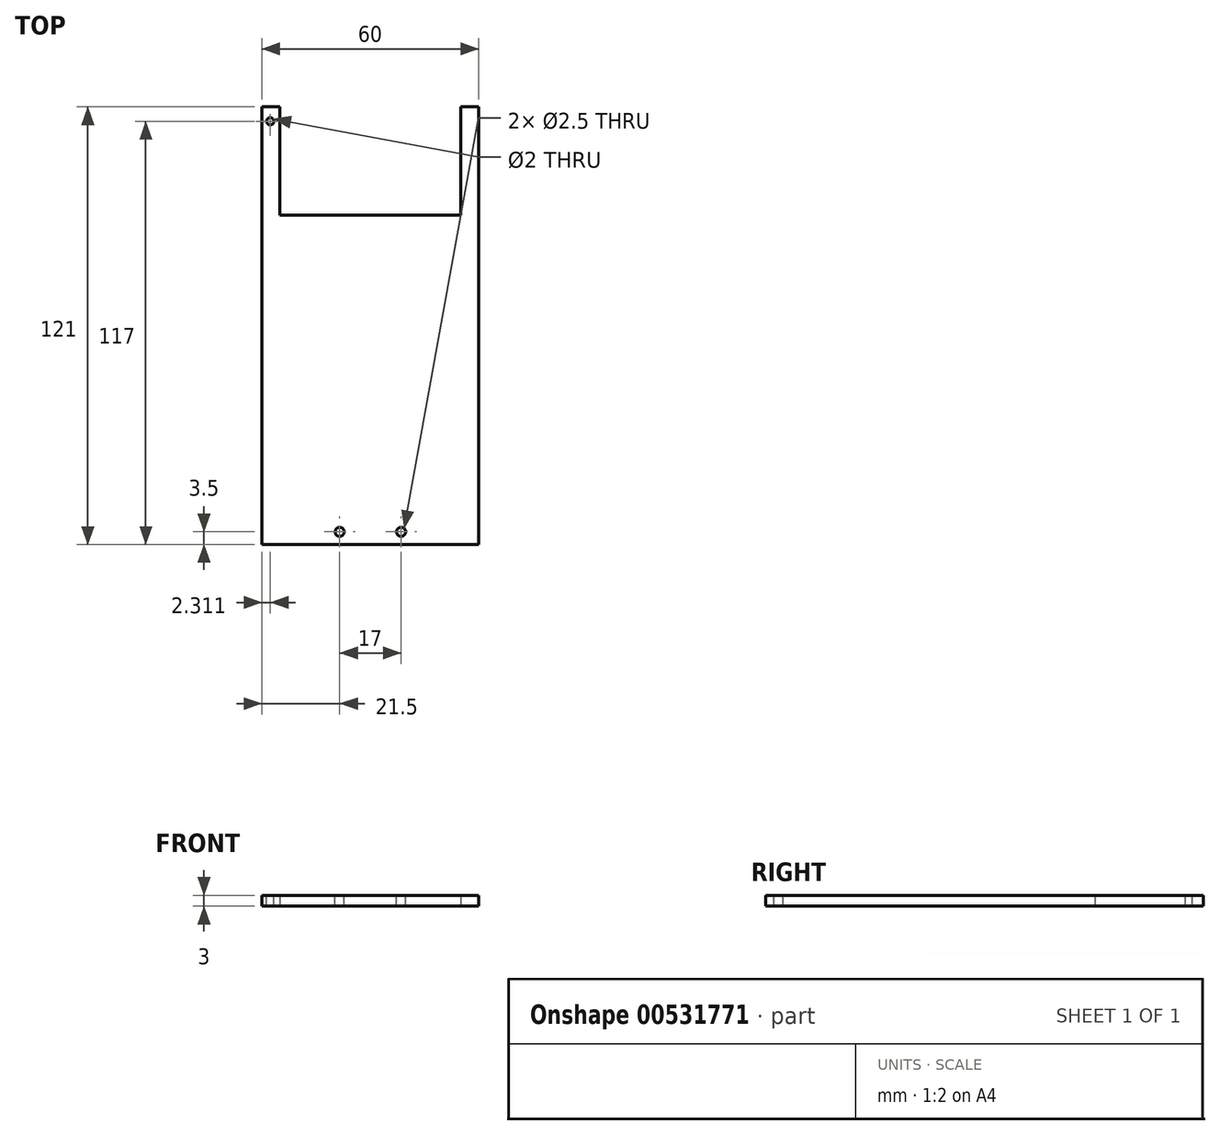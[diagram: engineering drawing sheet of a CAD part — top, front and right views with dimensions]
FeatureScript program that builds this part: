
annotation { "Feature Type Name" : "Feature", "Feature Type Description" : "" }
export const myFeature = defineFeature(function(context is Context, id is Id, definition is map)
    precondition{}
    {
        {
            var Q0;
            Q0=qCreatedBy(makeId("Top.planeOp"),FACE);
            var sketch = newSketch(context, id + "F0", { "sketchPlane" : qUnion([Q0])});
            skLineSegment(sketch, "E0.bottom", {"start": v(-30, 60.5) * mm, "end": v(30, 60.5) * mm});
            skLineSegment(sketch, "E0.top", {"start": v(-30, -60.5) * mm, "end": v(30, -60.5) * mm});
            skLineSegment(sketch, "E0.left", {"start": v(-30, 60.5) * mm, "end": v(-30, -60.5) * mm});
            skLineSegment(sketch, "E0.right", {"start": v(30, 60.5) * mm, "end": v(30, -60.5) * mm});
            skPoint(sketch, "E0.middle", {"position": v(0, 0) * mm});
            skLineSegment(sketch, "E1", {"start": v(-25, 60.5) * mm, "end": v(-25, 30.5) * mm});
            skLineSegment(sketch, "E2", {"start": v(-25, 30.5) * mm, "end": v(25, 30.5) * mm});
            skLineSegment(sketch, "E3", {"start": v(25, 30.5) * mm, "end": v(25, 60.5) * mm});
            skSolve(sketch);
        }
        {
            var Q0;
            Q0=makeQuery(id+"F0.imprint","IMPRINT",FACE,{"disambiguationData":[TD([[makeQuery(id+"F0.imprint","IMPRINT",EDGE,{"derivedFrom":sQuery(id+"F0.wireOp",EDGE,"E0.top")}),1.0]])]});
            extrude(context, id + "F1", {"entities" : qUnion([Q0]), "depth" : 2 * mm, "offsetDistance" : 25 * mm});
        }
        {
            var Q0;
            Q0=makeQuery(id+"F1.opExtrude","CAP_FACE",FACE,{"disambiguationData":[OSD([sQuery(id+"F0.wireOp",EDGE,"E0.bottom"),sQuery(id+"F0.wireOp",EDGE,"E0.top"),sQuery(id+"F0.wireOp",EDGE,"E0.left"),sQuery(id+"F0.wireOp",EDGE,"E0.right"),sQuery(id+"F0.wireOp",EDGE,"E1"),sQuery(id+"F0.wireOp",EDGE,"E2"),sQuery(id+"F0.wireOp",EDGE,"E3")])],"isStart":false});
            var sketch = newSketch(context, id + "F2", { "sketchPlane" : qUnion([Q0])});
            skCircle(sketch, "E4", {"center": v(-27.5, 57) * mm, "radius": 1 * mm});
            skSolve(sketch);
        }
        {
            var Q0;
            Q0=makeQuery(id+"F2.imprint","IMPRINT",FACE,{"disambiguationData":[TD([[makeQuery(id+"F2.imprint","IMPRINT",EDGE,{"derivedFrom":sQuery(id+"F2.wireOp",EDGE,"E4")}),1.0]])]});
            extrude(context, id + "F3", {"entities" : qUnion([Q0]), "operationType" : NewBodyOperationType.REMOVE, "oppositeDirection" : true, "depth" : 25 * mm, "offsetDistance" : 25 * mm});
        }
        {
            var Q0;
            Q0=makeQuery(id+"F0.imprint","IMPRINT",FACE,{"disambiguationData":[TD([[makeQuery(id+"F0.imprint","IMPRINT",EDGE,{"derivedFrom":sQuery(id+"F0.wireOp",EDGE,"E0.top")}),1.0]])]});
            extrude(context, id + "F4", {"entities" : qUnion([Q0]), "operationType" : NewBodyOperationType.ADD, "depth" : 3 * mm, "offsetDistance" : 25 * mm});
        }
        {
            var Q0;
            Q0=makeQuery(id+"F4.opExtrude","CAP_FACE",FACE,{"disambiguationData":[OSD([sQuery(id+"F0.wireOp",EDGE,"E0.bottom"),sQuery(id+"F0.wireOp",EDGE,"E0.top"),sQuery(id+"F0.wireOp",EDGE,"E0.left"),sQuery(id+"F0.wireOp",EDGE,"E0.right"),sQuery(id+"F0.wireOp",EDGE,"E1"),sQuery(id+"F0.wireOp",EDGE,"E2"),sQuery(id+"F0.wireOp",EDGE,"E3")])],"isStart":false});
            var sketch = newSketch(context, id + "F5", { "sketchPlane" : qUnion([Q0])});
            skLineSegment(sketch, "E5", {"start": v(-30, -60.5) * mm, "end": v(-30, 56.5) * mm});
            skCircle(sketch, "E6", {"center": v(-27.69, 56.5) * mm, "radius": 1 * mm});
            skSolve(sketch);
        }
        {
            var Q0;
            Q0=makeQuery(id+"F4.opExtrude","CAP_FACE",FACE,{"disambiguationData":[OSD([sQuery(id+"F0.wireOp",EDGE,"E0.bottom"),sQuery(id+"F0.wireOp",EDGE,"E0.top"),sQuery(id+"F0.wireOp",EDGE,"E0.left"),sQuery(id+"F0.wireOp",EDGE,"E0.right"),sQuery(id+"F0.wireOp",EDGE,"E1"),sQuery(id+"F0.wireOp",EDGE,"E2"),sQuery(id+"F0.wireOp",EDGE,"E3")])],"isStart":false});
            var sketch = newSketch(context, id + "F6", { "sketchPlane" : qUnion([Q0])});
            skLineSegment(sketch, "E7.bottom", {"start": v(-30, -60.5) * mm, "end": v(30, -60.5) * mm});
            skLineSegment(sketch, "E7.top", {"start": v(-30, -53.5) * mm, "end": v(30, -53.5) * mm});
            skLineSegment(sketch, "E7.left", {"start": v(-30, -60.5) * mm, "end": v(-30, -53.5) * mm});
            skLineSegment(sketch, "E7.right", {"start": v(30, -60.5) * mm, "end": v(30, -53.5) * mm});
            skLineSegment(sketch, "E8", {"start": v(-30, -60.5) * mm, "end": v(-12.5, -60.5) * mm});
            skLineSegment(sketch, "E9", {"start": v(30, -60.5) * mm, "end": v(12.5, -60.5) * mm});
            skLineSegment(sketch, "E10.bottom", {"start": v(-12.5, -60.5) * mm, "end": v(12.5, -60.5) * mm});
            skLineSegment(sketch, "E10.top", {"start": v(-12.5, -53.5) * mm, "end": v(12.5, -53.5) * mm});
            skCircle(sketch, "E11", {"center": v(-8.5, -57) * mm, "radius": 1.25 * mm});
            skCircle(sketch, "E12", {"center": v(8.5, -57) * mm, "radius": 1.25 * mm});
            skSolve(sketch);
        }
        {
            var Q0;
            Q0=makeQuery(id+"F6.imprint","IMPRINT",FACE,{"disambiguationData":[TD([[makeQuery(id+"F6.imprint","IMPRINT",EDGE,{"derivedFrom":sQuery(id+"F6.wireOp",EDGE,"E11")}),1.0]])]});
            var Q1;
            Q1=makeQuery(id+"F6.imprint","IMPRINT",FACE,{"disambiguationData":[TD([[makeQuery(id+"F6.imprint","IMPRINT",EDGE,{"derivedFrom":sQuery(id+"F6.wireOp",EDGE,"E12")}),1.0]])]});
            extrude(context, id + "F7", {"entities" : qUnion([Q0, Q1]), "operationType" : NewBodyOperationType.REMOVE, "oppositeDirection" : true, "depth" : 5 * mm, "offsetDistance" : 25 * mm});
        }
        {
            var Q0;
            Q0=makeQuery(id+"F5.imprint","IMPRINT",FACE,{"disambiguationData":[TD([[makeQuery(id+"F5.imprint","IMPRINT",EDGE,{"derivedFrom":sQuery(id+"F5.wireOp",EDGE,"E6")}),1.0]])]});
            extrude(context, id + "F8", {"entities" : qUnion([Q0]), "operationType" : NewBodyOperationType.REMOVE, "oppositeDirection" : true, "depth" : 25 * mm, "offsetDistance" : 25 * mm});
        }
    });
